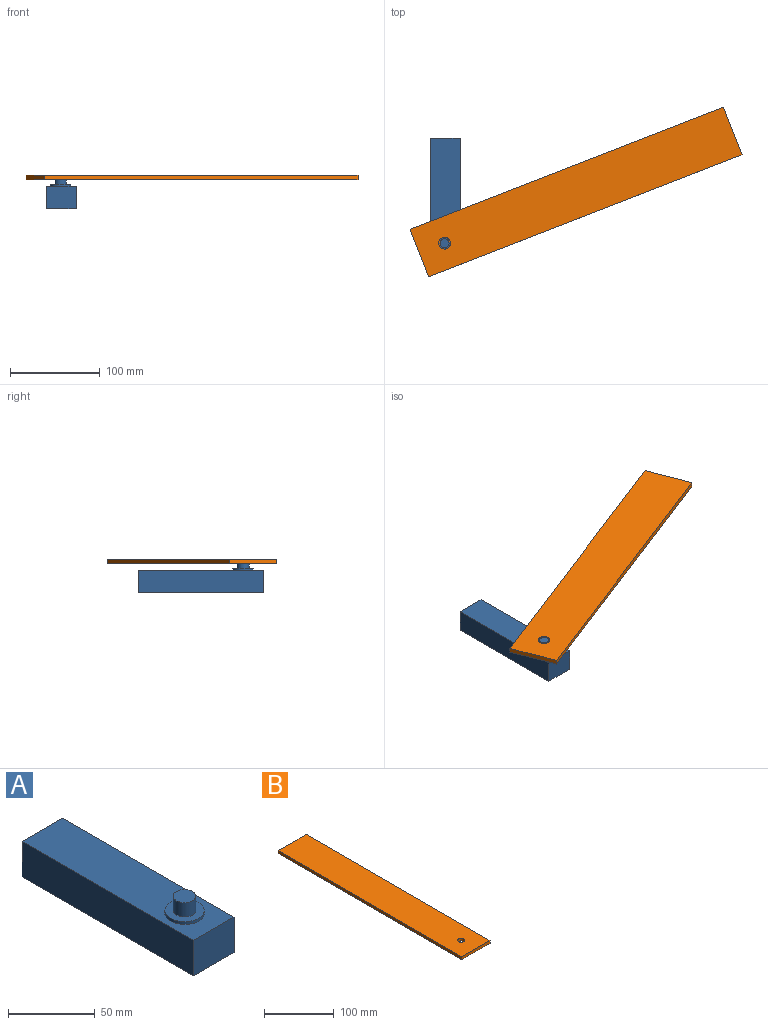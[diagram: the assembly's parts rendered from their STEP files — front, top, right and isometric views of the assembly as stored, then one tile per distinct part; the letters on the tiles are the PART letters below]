
ASSEMBLY  parts=2 mates=1
PART A: 10 faces, bbox 33x139.5x37 mm
  f0: plane 32.99x25mm, normal (0,1,0), area 824.7mm2, adj f1,f3,f4,f5
  f1: plane 139.52x25mm, normal (-1,0,0), area 3487.9mm2, adj f0,f2,f4,f5
  f2: plane 32.99x25mm, normal (0,-1,0), area 824.7mm2, adj f1,f3,f4,f5
  f3: plane 139.52x25mm, normal (1,0,0), area 3487.9mm2, adj f0,f2,f4,f5
  f4: plane 139.52x32.99mm, normal (0,0,1), area 4199.4mm2, adj f0,f1,f2,f3,f6
  f5: plane 139.52x32.99mm, normal (0,0,-1), area 4602.3mm2, adj f0,f1,f2,f3
  f6: cylinder r=11.33mm len=22.65mm, axis (0,0,-1), area 142.3mm2, adj f4,f7
  f7: plane 22.65x22.65mm, normal (0,0,1), area 267.3mm2, adj f6,f8
  f8: cylinder r=6.57mm len=13.14mm, axis (0,0,-1), area 412.9mm2, adj f7,f9
  f9: plane 13.14x13.14mm, normal (0,0,1), area 135.7mm2, adj f8
PART B: 7 faces, bbox 57x374.3x5 mm
  f0: plane 56.98x5mm, normal (0,-1,0), area 284.9mm2, adj f1,f3,f4,f5
  f1: plane 374.29x5mm, normal (1,0,0), area 1871.4mm2, adj f0,f2,f4,f5
  f2: plane 56.98x5mm, normal (0,1,0), area 284.9mm2, adj f1,f3,f4,f5
  f3: plane 374.29x5mm, normal (-1,0,0), area 1871.4mm2, adj f0,f2,f4,f5
  f4: plane 374.29x56.98mm, normal (0,0,1), area 21246.7mm2, adj f0,f1,f2,f3,f6
  f5: plane 374.29x56.98mm, normal (0,0,-1), area 21246.7mm2, adj f0,f1,f2,f3,f6
  f6: cylinder r=5mm len=10mm, axis (0,0,1), area 157.1mm2, adj f4,f5
PLACE A t=(-9.49,-5.71,-0.35)mm fixed
PLACE B rot(axis=(0,0,-1),68.7deg) t=(160.33,4.36,31.65)mm
MATE revolute B.f6 <-> A.f6  axis (0,0,1) through (14.05,-52.59,36.65)mm
